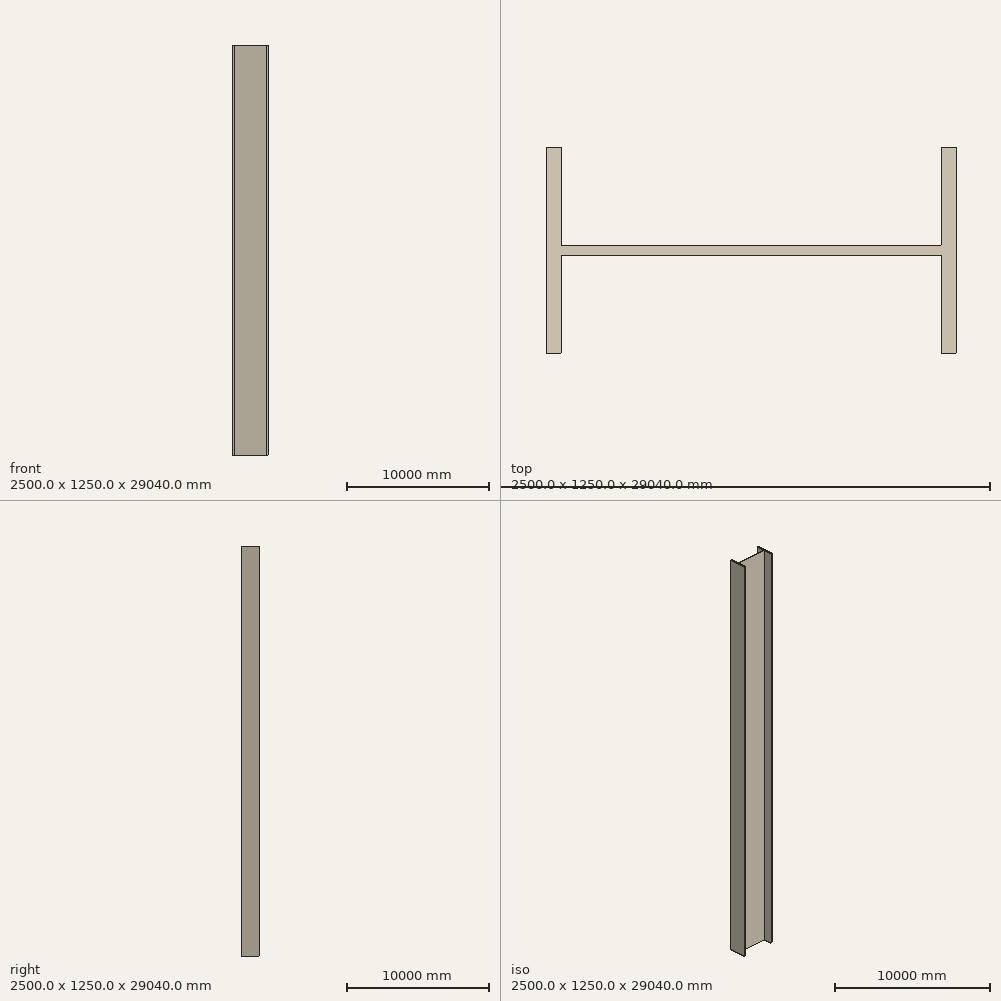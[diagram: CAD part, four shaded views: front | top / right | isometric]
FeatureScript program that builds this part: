
annotation { "Feature Type Name" : "Feature", "Feature Type Description" : "" }
export const myFeature = defineFeature(function(context is Context, id is Id, definition is map)
    precondition{}
    {
        {
            var Q0;
            Q0=qCreatedBy(makeId("Top.planeOp"),FACE);
            var sketch = newSketch(context, id + "F0", { "sketchPlane" : qUnion([Q0])});
            skLineSegment(sketch, "E0", {"start": v(1268.01, -18.56) * mm, "end": v(1268.01, 606.44) * mm});
            skLineSegment(sketch, "E1", {"start": v(1268.01, 606.44) * mm, "end": v(1178.01, 606.44) * mm});
            skLineSegment(sketch, "E2", {"start": v(1178.01, 606.44) * mm, "end": v(1178.01, 11.44) * mm});
            skLineSegment(sketch, "E3", {"start": v(1178.01, 11.44) * mm, "end": v(-1141.99, 11.44) * mm});
            skLineSegment(sketch, "E4", {"start": v(-1141.99, 11.44) * mm, "end": v(-1141.99, 606.44) * mm});
            skLineSegment(sketch, "E5", {"start": v(-1141.99, 606.44) * mm, "end": v(-1231.99, 606.44) * mm});
            skLineSegment(sketch, "E6", {"start": v(-1231.99, 606.44) * mm, "end": v(-1231.99, -18.56) * mm});
            skLineSegment(sketch, "E7.MirrorCS", {"start": v(1268.01, -643.56) * mm, "end": v(1178.01, -643.56) * mm});
            skLineSegment(sketch, "E8.MirrorCS", {"start": v(-1141.99, -643.56) * mm, "end": v(-1231.99, -643.56) * mm});
            skLineSegment(sketch, "E9.MirrorCS", {"start": v(1268.01, -18.56) * mm, "end": v(1268.01, -643.56) * mm});
            skLineSegment(sketch, "E10.MirrorCS", {"start": v(1178.01, -643.56) * mm, "end": v(1178.01, -48.56) * mm});
            skLineSegment(sketch, "E11.MirrorCS", {"start": v(-1231.99, -643.56) * mm, "end": v(-1231.99, -18.56) * mm});
            skLineSegment(sketch, "E12.MirrorCS", {"start": v(-1141.99, -48.56) * mm, "end": v(-1141.99, -643.56) * mm});
            skLineSegment(sketch, "E13.MirrorCS", {"start": v(1178.01, -48.56) * mm, "end": v(-1141.99, -48.56) * mm});
            skSolve(sketch);
        }
        {
            var Q0;
            Q0=makeQuery(id+"F0.imprint","IMPRINT",FACE,{"disambiguationData":[TD([[makeQuery(id+"F0.imprint","IMPRINT",EDGE,{"derivedFrom":sQuery(id+"F0.wireOp",EDGE,"E0")}),1.0]])]});
            extrude(context, id + "F1", {"entities" : qUnion([Q0]), "oppositeDirection" : true, "depth" : 29040 * mm, "offsetDistance" : 25 * mm});
        }
    });
